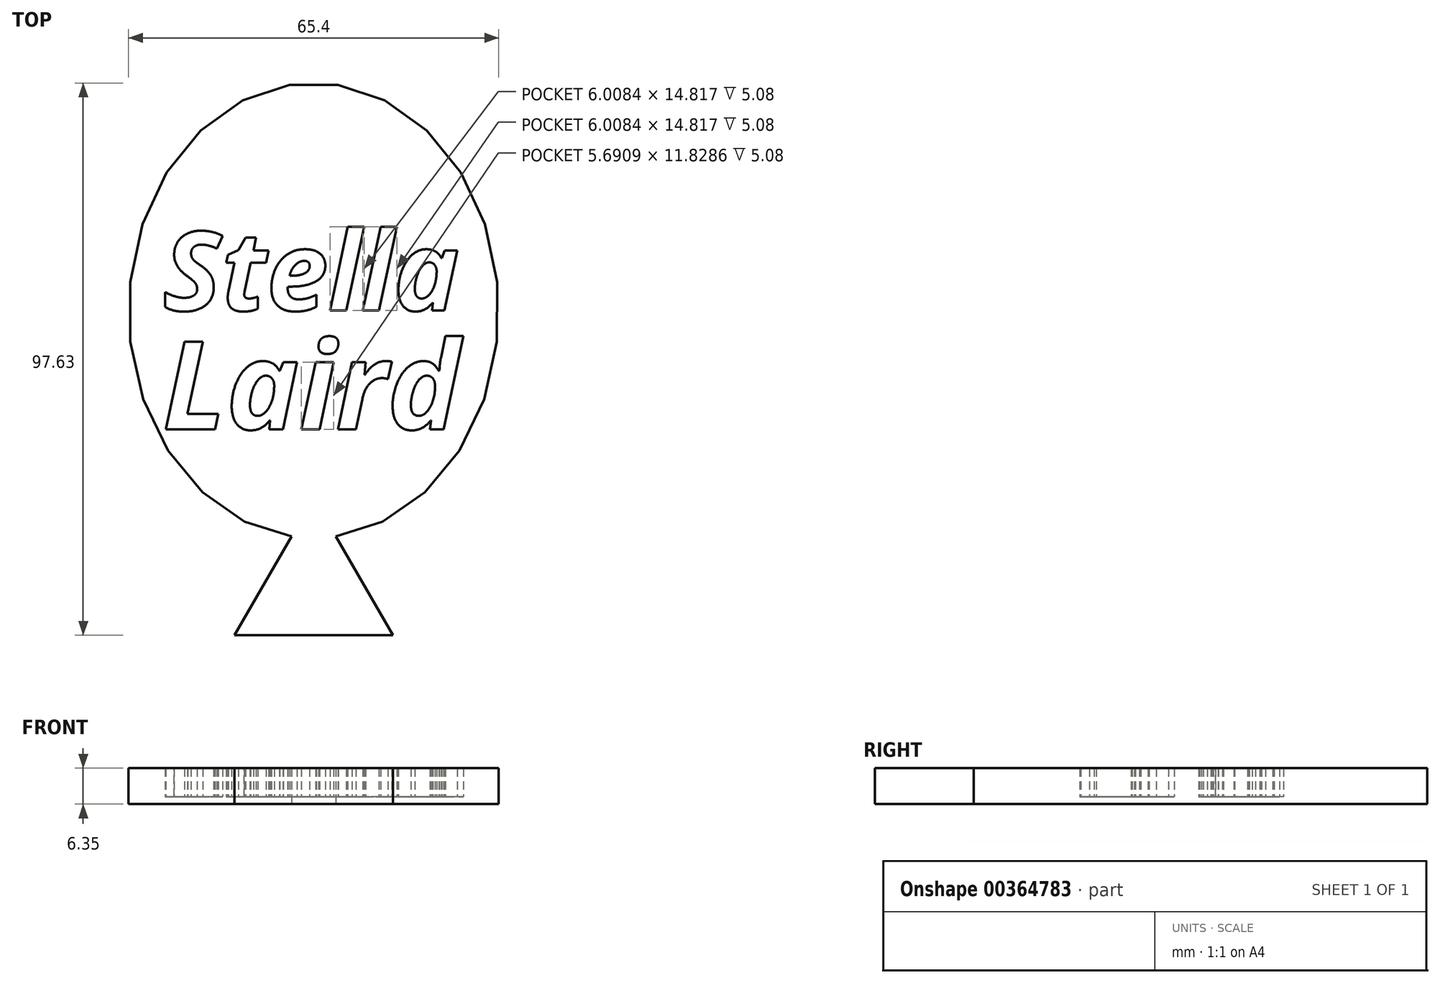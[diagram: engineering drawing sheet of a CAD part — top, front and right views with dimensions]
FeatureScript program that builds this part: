
annotation { "Feature Type Name" : "Feature", "Feature Type Description" : "" }
export const myFeature = defineFeature(function(context is Context, id is Id, definition is map)
    precondition{}
    {
        {
            var Q0;
            Q0=qCreatedBy(makeId("Top.planeOp"),FACE);
            var sketch = newSketch(context, id + "F0", { "sketchPlane" : qUnion([Q0])});
            skEllipse(sketch, "E0", {"center": v(0, 0) * mm, "majorRadius": 40.22 * mm, "minorRadius": 32.7 * mm, "majorAxis": v(0, 1)});
            skText(sketch, "E1", { "text": "Stella", "fontName": "OpenSans-BoldItalic.ttf"});
            skPoint(sketch, "E1.secondSnap0", {"position": v(-32.7, 0) * mm});
            skText(sketch, "E2", { "text": "Laird", "fontName": "OpenSans-BoldItalic.ttf"});
            skPoint(sketch, "E3", {"position": v(0, -40.22) * mm});
            skCircle(sketch, "E4.cCircle", {"center": v(0, -49.33) * mm, "radius": 8.08 * mm, "construction": true});
            skLineSegment(sketch, "E4.0", {"start": v(13.99, -57.4) * mm, "end": v(-13.99, -57.4) * mm});
            skLineSegment(sketch, "E4.1", {"start": v(-13.99, -57.4) * mm, "end": v(0, -33.18) * mm});
            skLineSegment(sketch, "E4.2", {"start": v(0, -33.18) * mm, "end": v(13.99, -57.4) * mm});
            skPoint(sketch, "E4.0.midPoint", {"position": v(0, -57.4) * mm});
            const initialGuessF0  = {"E1": [-0.02665, 0, 1, 0, 0.01404], "E2": [-0.02665, -0.02098, 1, 0, 0.0156]};
            skSetInitialGuess(sketch, initialGuessF0);
            skSolve(sketch);
        }
        {
            var Q0;
            Q0=makeQuery(id+"F0.imprint","IMPRINT",FACE,{"disambiguationData":[TD([[makeQuery(id+"F0.imprint","IMPRINT",EDGE,{"derivedFrom":sQuery(id+"F0.wireOp",EDGE,"E1.sketch_text.stroke-0")}),1.0]])]});
            var Q1;
            {var subQ5=sQuery(id+"F0.wireOp",EDGE,"E4.0");Q1=makeQuery(id+"F0.imprint","IMPRINT",FACE,{"disambiguationData":[TD([[makeQuery(id+"F0.imprint","IMPRINT",EDGE,{"derivedFrom":subQ5}),-1.0]])]});}
            var Q2;
            {var subQ0=sQuery(id+"F0.wireOp",EDGE,"E4.1");var subQ1=sQuery(id+"F0.wireOp",EDGE,"E0");var subQ2=makeQuery(id+"F0.imprint","INTERSECT",VERTEX,{"derivedFrom":[subQ1,subQ0]});Q2=makeQuery(id+"F0.imprint","IMPRINT",FACE,{"disambiguationData":[TD([[makeQuery(id+"F0.imprint","IMPRINT",EDGE,{"disambiguationData":[TD([[subQ2,-1.0]])],"derivedFrom":subQ1}),1.0]])]});}
            var Q3;
            Q3=makeQuery(id+"F0.imprint","IMPRINT",FACE,{"disambiguationData":[TD([[makeQuery(id+"F0.imprint","IMPRINT",EDGE,{"derivedFrom":sQuery(id+"F0.wireOp",EDGE,"E1.sketch_text.stroke-43")}),1.0]])]});
            var Q4;
            Q4=makeQuery(id+"F0.imprint","IMPRINT",FACE,{"disambiguationData":[TD([[makeQuery(id+"F0.imprint","IMPRINT",EDGE,{"derivedFrom":sQuery(id+"F0.wireOp",EDGE,"E1.sketch_text.stroke-90")}),1.0]])]});
            var Q5;
            Q5=makeQuery(id+"F0.imprint","IMPRINT",FACE,{"disambiguationData":[TD([[makeQuery(id+"F0.imprint","IMPRINT",EDGE,{"derivedFrom":sQuery(id+"F0.wireOp",EDGE,"E2.sketch_text.stroke-21")}),1.0]])]});
            var Q6;
            Q6=makeQuery(id+"F0.imprint","IMPRINT",FACE,{"disambiguationData":[TD([[makeQuery(id+"F0.imprint","IMPRINT",EDGE,{"derivedFrom":sQuery(id+"F0.wireOp",EDGE,"E2.sketch_text.stroke-72")}),1.0]])]});
            extrude(context, id + "F1", {"entities" : qUnion([Q0, Q1, Q2, Q3, Q4, Q5, Q6]), "depth" : 6.35 * mm});
        }
        {
            var Q0;
            Q0=makeQuery(id+"F0.imprint","IMPRINT",FACE,{"disambiguationData":[TD([[makeQuery(id+"F0.imprint","IMPRINT",EDGE,{"derivedFrom":sQuery(id+"F0.wireOp",EDGE,"E1.sketch_text.stroke-43")}),-1.0]])]});
            var Q1;
            Q1=makeQuery(id+"F0.imprint","IMPRINT",FACE,{"disambiguationData":[TD([[makeQuery(id+"F0.imprint","IMPRINT",EDGE,{"derivedFrom":sQuery(id+"F0.wireOp",EDGE,"E1.sketch_text.stroke-67")}),-1.0]])]});
            var Q2;
            Q2=makeQuery(id+"F0.imprint","IMPRINT",FACE,{"disambiguationData":[TD([[makeQuery(id+"F0.imprint","IMPRINT",EDGE,{"derivedFrom":sQuery(id+"F0.wireOp",EDGE,"E1.sketch_text.stroke-71")}),-1.0]])]});
            var Q3;
            Q3=makeQuery(id+"F0.imprint","IMPRINT",FACE,{"disambiguationData":[TD([[makeQuery(id+"F0.imprint","IMPRINT",EDGE,{"derivedFrom":sQuery(id+"F0.wireOp",EDGE,"E1.sketch_text.stroke-75")}),-1.0]])]});
            var Q4;
            Q4=makeQuery(id+"F0.imprint","IMPRINT",FACE,{"disambiguationData":[TD([[makeQuery(id+"F0.imprint","IMPRINT",EDGE,{"derivedFrom":sQuery(id+"F0.wireOp",EDGE,"E1.sketch_text.stroke-24")}),-1.0]])]});
            var Q5;
            Q5=makeQuery(id+"F0.imprint","IMPRINT",FACE,{"disambiguationData":[TD([[makeQuery(id+"F0.imprint","IMPRINT",EDGE,{"derivedFrom":sQuery(id+"F0.wireOp",EDGE,"E1.sketch_text.stroke-0")}),-1.0]])]});
            var Q6;
            Q6=makeQuery(id+"F0.imprint","IMPRINT",FACE,{"disambiguationData":[TD([[makeQuery(id+"F0.imprint","IMPRINT",EDGE,{"derivedFrom":sQuery(id+"F0.wireOp",EDGE,"E2.sketch_text.stroke-0")}),-1.0]])]});
            var Q7;
            Q7=makeQuery(id+"F0.imprint","IMPRINT",FACE,{"disambiguationData":[TD([[makeQuery(id+"F0.imprint","IMPRINT",EDGE,{"derivedFrom":sQuery(id+"F0.wireOp",EDGE,"E2.sketch_text.stroke-6")}),-1.0]])]});
            var Q8;
            Q8=makeQuery(id+"F0.imprint","IMPRINT",FACE,{"disambiguationData":[TD([[makeQuery(id+"F0.imprint","IMPRINT",EDGE,{"derivedFrom":sQuery(id+"F0.wireOp",EDGE,"E2.sketch_text.stroke-21")}),1.0]])]});
            var Q9;
            Q9=makeQuery(id+"F0.imprint","IMPRINT",FACE,{"disambiguationData":[TD([[makeQuery(id+"F0.imprint","IMPRINT",EDGE,{"derivedFrom":sQuery(id+"F0.wireOp",EDGE,"E2.sketch_text.stroke-38")}),-1.0]])]});
            var Q10;
            Q10=makeQuery(id+"F0.imprint","IMPRINT",FACE,{"disambiguationData":[TD([[makeQuery(id+"F0.imprint","IMPRINT",EDGE,{"derivedFrom":sQuery(id+"F0.wireOp",EDGE,"E2.sketch_text.stroke-31")}),-1.0]])]});
            var Q11;
            Q11=makeQuery(id+"F0.imprint","IMPRINT",FACE,{"disambiguationData":[TD([[makeQuery(id+"F0.imprint","IMPRINT",EDGE,{"derivedFrom":sQuery(id+"F0.wireOp",EDGE,"E2.sketch_text.stroke-42")}),-1.0]])]});
            var Q12;
            Q12=makeQuery(id+"F0.imprint","IMPRINT",FACE,{"disambiguationData":[TD([[makeQuery(id+"F0.imprint","IMPRINT",EDGE,{"derivedFrom":sQuery(id+"F0.wireOp",EDGE,"E2.sketch_text.stroke-54")}),-1.0]])]});
            var Q13;
            Q13=makeQuery(id+"F0.imprint","IMPRINT",FACE,{"disambiguationData":[TD([[makeQuery(id+"F0.imprint","IMPRINT",EDGE,{"derivedFrom":sQuery(id+"F0.wireOp",EDGE,"E2.sketch_text.stroke-72")}),1.0]])]});
            var Q14;
            Q14=makeQuery(id+"F0.imprint","IMPRINT",FACE,{"disambiguationData":[TD([[makeQuery(id+"F0.imprint","IMPRINT",EDGE,{"derivedFrom":sQuery(id+"F0.wireOp",EDGE,"E1.sketch_text.stroke-90")}),1.0]])]});
            var Q15;
            Q15=makeQuery(id+"F0.imprint","IMPRINT",FACE,{"disambiguationData":[TD([[makeQuery(id+"F0.imprint","IMPRINT",EDGE,{"derivedFrom":sQuery(id+"F0.wireOp",EDGE,"E1.sketch_text.stroke-43")}),1.0]])]});
            extrude(context, id + "F2", {"entities" : qUnion([Q0, Q1, Q2, Q3, Q4, Q5, Q6, Q7, Q8, Q9, Q10, Q11, Q12, Q13, Q14, Q15]), "operationType" : NewBodyOperationType.ADD, "depth" : 1.27 * mm});
        }
    });
